# Revit family: M_Upper Cabinet-Double Door-Wall (415 MITRE FVP edit)
name_source: partatom
category: Casework
revit_build: Autodesk Revit 2014 (Build: 20130722_2115(x64)
units: mm (PartAtom-declared; Revit-internal decimal feet)

## types (5) — shared parameters
Handle Material = Cabinets - Handles
Top Of Cabinet = 2000 mm  [stored 6.56168 ft]

## per-type parameters (varying)
| type | Cabinet Material | Depth | Door/Drawer Material | Height | Width |
| 600mm | <By Category> | 300 mm | <By Category> | 600 mm | 600 mm |
| 1000mm | <By Category> | 660 mm | Paint (off white) | 473 mm | 927 mm |
| 1000mm 4 | Paint (off white) | 381 mm  [stored 1.25 ft] | Paint (off white) | 991 mm | 847 mm |
| 1000mm 3 | Paint (off white) | 381 mm  [stored 1.25 ft] | Paint (off white) | 841 mm | 787 mm |
| 1000mm 2 | Paint (off white) | 381 mm  [stored 1.25 ft] | Paint (off white) | 534 mm | 610 mm |

note: [stored X ft] marks values corroborated as IEEE doubles in the binary element streams (Revit-internal decimal feet)
